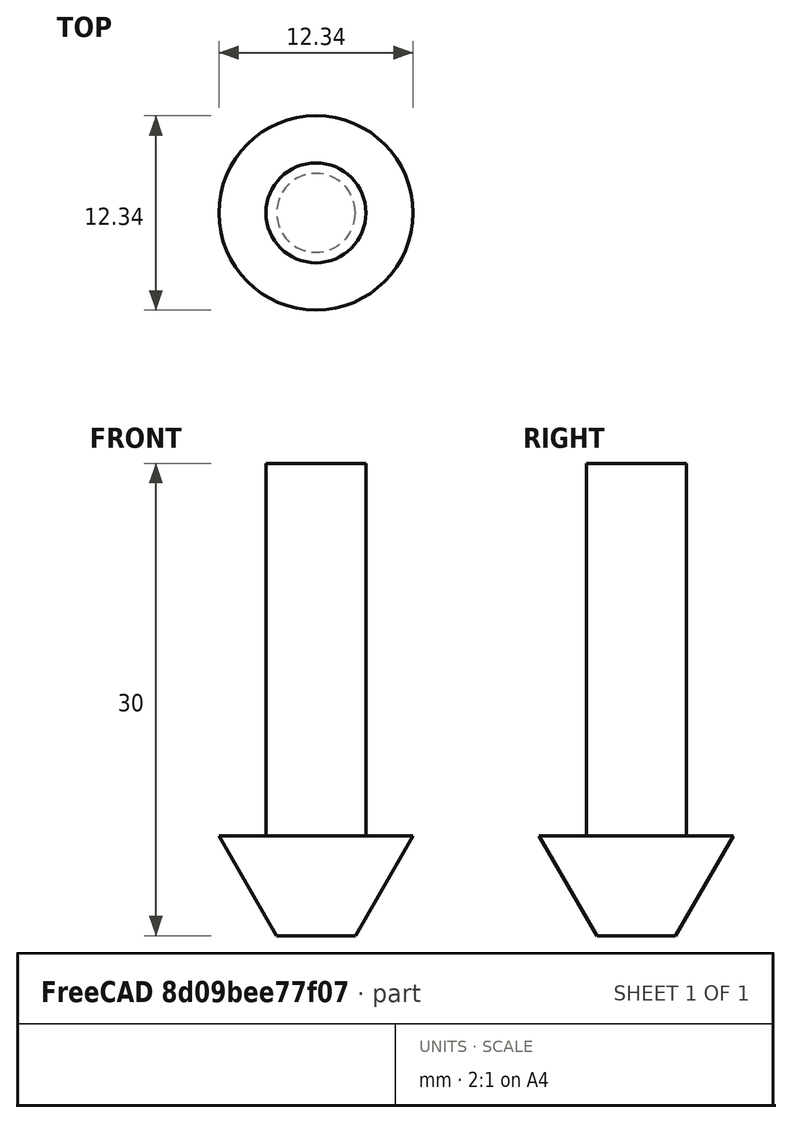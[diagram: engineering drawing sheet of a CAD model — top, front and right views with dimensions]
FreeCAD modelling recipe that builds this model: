
FCSTD DOCUMENT  (FreeCAD 0.20R26155 (Git))
Label: chamfer-fixed
License: All rights reserved
LicenseURL: http://en.wikipedia.org/wiki/All_rights_reserved
objects: Sketcher::SketchObject×1, PartDesign::Revolution×1, App::FeaturePython×1, PartDesign::Body×1
note: 4 computed .brp shape members not serialized (recipe doc carries the construction recipe); baked Part::Feature solids carry a one-line shape summary decoded from their .brp

FEATURE [Sketcher::SketchObject] Sketch
  FullyConstrained = true
  MapMode = 5
  Placement = pos=(0,0,0) rot=(1,0,0;1.5708rad)
  Support = -> [XZ_Plane]
  expr: Constraints[5] = <<Attributes>>.Length
  expr: Constraints[10] = <<Attributes>>.CuttingEdgeHeight
  expr: Constraints[13] = <<Attributes>>.ShankDiameter / 2
  expr: Constraints[14] = <<Attributes>>.TipDiameter / 2 + 1um
  expr: Constraints[16] = <<Attributes>>.CuttingEdgeAngle / 2
  sketch-geometry (6):
    g0: LineSegment StartX=0 StartY=30 StartZ=0 EndX=0 EndY=0 EndZ=0
    g1: LineSegment StartX=0 StartY=0 StartZ=0 EndX=2.501 EndY=0 EndZ=0
    g2: LineSegment StartX=2.501 StartY=0 StartZ=0 EndX=6.16717 EndY=6.35 EndZ=0
    g3: LineSegment StartX=3.175 StartY=30 StartZ=0 EndX=0 EndY=30 EndZ=0
    g4: LineSegment StartX=3.175 StartY=6.36 StartZ=0 EndX=6.16717 EndY=6.35 EndZ=0
    g5: LineSegment StartX=3.175 StartY=30 StartZ=0 EndX=3.175 EndY=6.36 EndZ=0
  constraints (17):
    c: Vertical(g0)
    c: Coincident(g0,g1)
    c: Horizontal(g1)
    c: Coincident(g1,g2)
    c: Horizontal(g3)
    c: DistanceY(g2,g3) = 30
    c: Coincident(g2,g4)
    c: Vertical(g5)
    c: Coincident(g3,g5)
    c: Coincident(g4,g5)
    c: DistanceY(g2) = 6.35
    c: Coincident(g0,g-1)
    c: Coincident(g0,g3)
    c: DistanceX(g-2,g3) = 3.175
    c: DistanceX(g-2,g1) = 2.501
    c: DistanceY(g2,g4) = 0.01
    c: Angle(g2,g-2) = 0.523599
FEATURE [PartDesign::Revolution] Revolution
  AllowMultiFace = false
  Angle = 360
  Axis = (0,-2e-16,1)
  Base = (0,0,0)
  Placement = pos=(0,0,0) rot=(1,0,0;1.5708rad)
  Profile = -> Sketch
  ReferenceAxis = -> Sketch [V_Axis]
  Reversed = true
FEATURE [App::FeaturePython] PropertyBag  label="Attributes"  # WARN: FeaturePython — macro-defined, semantics opaque (R4)
  Chipload = 0
  CustomPropertyGroups = Attributes | Shape
  CuttingEdgeAngle = 60
  CuttingEdgeHeight = 6.35
  Diameter = 12
  Flutes = 0
  Length = 30
  Material = 0
  ShankDiameter = 6.35
  TipDiameter = 5
FEATURE [PartDesign::Body] Body  label="ChamferTool"
  Group = -> [Sketch,Revolution,PropertyBag]
  Origin = -> Origin
  Tip = -> Revolution
